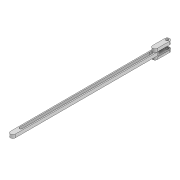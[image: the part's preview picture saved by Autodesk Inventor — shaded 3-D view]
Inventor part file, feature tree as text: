
AUTODESK INVENTOR PART (.ipt)
format: ipt  version: 2022 (Build 260153000, 153)  size: 156,160 bytes
history: native  units: mm
features: extrude x6, sketch x5, projected_geometry x4
ambient origin geometry x8: Origin, YZ Plane, XZ Plane, XY Plane, X Axis, Y Axis, Z Axis, Center Point
bodies: Solid1 (feature_tree)
feature tree (15):
  extrude  "Extrusion1"  Depth=6.0mm
  sketch  "Sketch2"  dims[d3=189.937mm d6=4.0mm d7=0.0mm]
  extrude  "Extrusion2"  Depth=4.0mm TaperAngle=0.0deg
  extrude  "Extrusion3"  Depth=3.2mm
  extrude  "Extrusion4"  Depth=10.0mm
  extrude  "Extrusion5"  Depth=4.0mm TaperAngle=0.0deg
  extrude  "Extrusion6"  Depth=6.0mm
  sketch  "Sketch1"  dims[d1=3.2mm d2=6.0mm]
  projected_geometry  "Projected Loop1"
  sketch  "Sketch3"  dims[d16=3.2mm d17=20.0mm]
  projected_geometry  "Projected Loop2"
  sketch  "Sketch4"  dims[d18=10.0mm d20=15.0mm]
  projected_geometry  "Projected Loop3"
  sketch  "Sketch5"  dims[d21=6.0mm d22=4.0mm d23=0.0mm d24=6.0mm d25=15.0mm d26=4.0mm d27=0.0mm d28=5.0mm d29=0.0mm d30=0.2mm d31=0.0mm d32=0.2mm d33=0.0mm]
  projected_geometry  "Projected Loop4"
